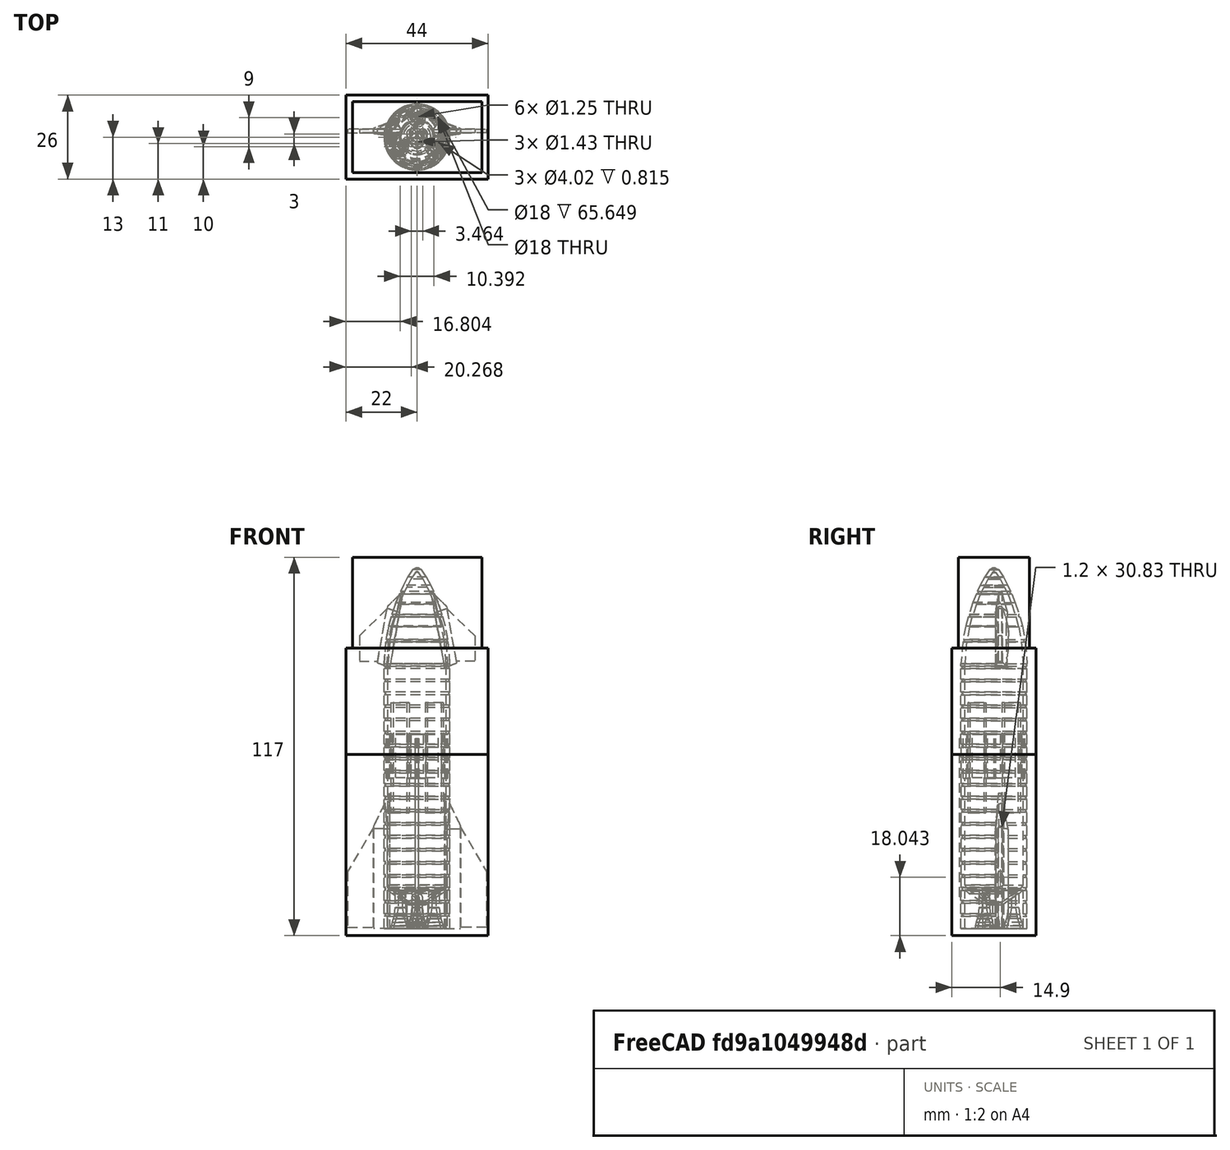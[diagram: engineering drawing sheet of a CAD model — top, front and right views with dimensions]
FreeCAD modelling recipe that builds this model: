
FCSTD DOCUMENT  (FreeCAD 0.18R16146 (Git))
Label: starship
License: All rights reserved
LicenseURL: http://en.wikipedia.org/wiki/All_rights_reserved
objects: Sketcher::SketchObject×14, Part::FeaturePython×5, Part::Box×5, Part::Extrusion×4, Part::Torus×4, Part::Revolution×4, Part::MultiFuse×4, Mesh::Feature×2, Part::Loft×2, Image::ImagePlane×1, Part::Cylinder×1, Part::Compound×1, PartDesign::FeatureBase×1, PartDesign::Body×1, Part::Mirroring×1, Part::Cut×1
note: 48 computed .brp shape members not serialized (recipe doc carries the construction recipe); baked Part::Feature solids carry a one-line shape summary decoded from their .brp

FEATURE [Mesh::Feature] SN8_Core
FEATURE [Mesh::Feature] SN8_Nose
  Placement = pos=(10.7,-34,-164.97) rot=(0,1,0;3.14159rad)
FEATURE [Image::ImagePlane] ImagePlane
  Placement = pos=(0,17,0) rot=(1,0,0;1.5708rad)
  XSize = 93
  YSize = 130
FEATURE [Sketcher::SketchObject] Sketch  label="fuse"
  Placement = pos=(0,0,0) rot=(1,0,0;1.5708rad)
  sketch-geometry (12):
    g0: LineSegment StartX=1.39017 StartY=57.1876 StartZ=0 EndX=2.9316 EndY=54.8754 EndZ=0
    g1: LineSegment StartX=5.37975 StartY=50.0245 StartZ=0 EndX=6.55849 EndY=46.987 EndZ=0
    g2: LineSegment StartX=6.55849 StartY=46.987 StartZ=0 EndX=7.91857 EndY=42.9067 EndZ=0
    g3: LineSegment StartX=7.91857 StartY=42.9067 StartZ=0 EndX=8.78321 EndY=39.8104 EndZ=0
    g4: LineSegment StartX=8.78321 StartY=39.8104 StartZ=0 EndX=9.64459 EndY=35.1408 EndZ=0
    g5: LineSegment StartX=9.64459 StartY=35.1408 StartZ=0 EndX=10.2 EndY=28.1137 EndZ=0
    g6: LineSegment StartX=10.2 StartY=28.1137 StartZ=0 EndX=10.2 EndY=25.3049 EndZ=0
    g7: LineSegment StartX=10.2 StartY=25.3049 StartZ=0 EndX=10.2 EndY=-53.7768 EndZ=0
    g8: LineSegment StartX=1.39017 StartY=57.1876 StartZ=0 EndX=0.452917 EndY=57.777 EndZ=0
    g9: LineSegment StartX=0.452917 StartY=57.777 StartZ=0 EndX=0 EndY=57.777 EndZ=0
    g10: LineSegment StartX=2.9316 StartY=54.8754 StartZ=0 EndX=4.24635 EndY=52.3366 EndZ=0
    g11: LineSegment StartX=4.24635 StartY=52.3366 StartZ=0 EndX=5.37975 EndY=50.0245 EndZ=0
  constraints (16):
    c: Coincident(g1,g2)
    c: Coincident(g2,g3)
    c: Coincident(g3,g4)
    c: Coincident(g4,g5)
    c: Coincident(g5,g6)
    c: Coincident(g6,g7)
    c: Vertical(g7)
    c: Coincident(g0,g8)
    c: Coincident(g8,g9)
    c: Horizontal(g9)
    c: Coincident(g0,g10)
    c: Coincident(g11,g1)
    c: Coincident(g10,g11)
    c: Vertical(g6)
    c: DistanceX(g-1,g7) = 10.2
    c: PointOnObject(g9,g-2)
FEATURE [Sketcher::SketchObject] Sketch001  label="bulkhead"
  Placement = pos=(0,0,0) rot=(-1,0,0;4.71239rad)
  sketch-geometry (5):
    g0: LineSegment StartX=10.1563 StartY=-38.9984 StartZ=0 EndX=9.76929 EndY=-40.6281 EndZ=0
    g1: LineSegment StartX=9.76929 StartY=-40.6281 StartZ=0 EndX=8.91371 EndY=-41.9522 EndZ=0
    g2: LineSegment StartX=8.91371 StartY=-41.9522 StartZ=0 EndX=7.7322 EndY=-42.9503 EndZ=0
    g3: LineSegment StartX=7.7322 StartY=-42.9503 StartZ=0 EndX=2.558 EndY=-46.4338 EndZ=0
    g4: LineSegment StartX=2.558 StartY=-46.4338 StartZ=0 EndX=0 EndY=-46.4338 EndZ=0
  constraints (6):
    c: Coincident(g0,g1)
    c: Coincident(g1,g2)
    c: Coincident(g2,g3)
    c: Coincident(g3,g4)
    c: Horizontal(g4)
    c: PointOnObject(g4,g-2)
FEATURE [Sketcher::SketchObject] Sketch002
  Placement = pos=(0,0,0) rot=(-1,0,0;4.71239rad)
  sketch-geometry (6):
    g0: LineSegment StartX=9.20478 StartY=45.2053 StartZ=0 EndX=17.8355 EndY=36.6962 EndZ=0
    g1: LineSegment StartX=17.8355 StartY=36.6962 StartZ=0 EndX=17.8355 EndY=28.9468 EndZ=0
    g2: LineSegment StartX=17.8355 StartY=28.9468 StartZ=0 EndX=12.0918 EndY=28.9468 EndZ=0
    g3: LineSegment StartX=12.0918 StartY=28.9468 StartZ=0 EndX=11.0282 EndY=28.7036 EndZ=0
    g4: LineSegment StartX=11.0282 StartY=28.7036 StartZ=0 EndX=7.9588 EndY=45.6004 EndZ=0
    g5: LineSegment StartX=7.9588 StartY=45.6004 StartZ=0 EndX=9.20478 EndY=45.2053 EndZ=0
  constraints (8):
    c: Coincident(g0,g1)
    c: Vertical(g1)
    c: Coincident(g1,g2)
    c: Horizontal(g2)
    c: Coincident(g2,g3)
    c: Coincident(g3,g4)
    c: Coincident(g4,g5)
    c: Coincident(g0,g5)
FEATURE [Part::Extrusion] Extrude  label="canard"
  Base = -> Sketch002
  Dir = (0,-1,0)
  DirMode = 2
  FaceMakerClass = Part::FaceMakerBullseye
  LengthFwd = 1.2
  LengthRev = 0
  Placement = pos=(0,2.5,0) rot=(0,0,1;0rad)
  Solid = true
  Symmetric = false
FEATURE [Sketcher::SketchObject] Sketch003
  Placement = pos=(0,0,0) rot=(-1,0,0;4.71239rad)
  sketch-geometry (5):
    g0: LineSegment StartX=11.6943 StartY=-21.9919 StartZ=0 EndX=13.1785 EndY=-21.9919 EndZ=0
    g1: LineSegment StartX=13.1785 StartY=-21.9919 StartZ=0 EndX=21.419 EndY=-36.1383 EndZ=0
    g2: LineSegment StartX=21.419 StartY=-36.1383 StartZ=0 EndX=21.419 EndY=-53.3693 EndZ=0
    g3: LineSegment StartX=21.419 StartY=-53.3693 StartZ=0 EndX=11.6943 EndY=-53.3693 EndZ=0
    g4: LineSegment StartX=11.6943 StartY=-53.3693 StartZ=0 EndX=11.6943 EndY=-21.9919 EndZ=0
  constraints (9):
    c: Horizontal(g0)
    c: Coincident(g0,g1)
    c: Coincident(g1,g2)
    c: Vertical(g2)
    c: Coincident(g2,g3)
    c: Horizontal(g3)
    c: Coincident(g3,g4)
    c: Coincident(g4,g0)
    c: Vertical(g4)
FEATURE [Part::Extrusion] Extrude001  label="wing"
  Base = -> Sketch003
  Dir = (0,-1,0)
  DirMode = 2
  FaceMakerClass = Part::FaceMakerBullseye
  LengthFwd = 1.2
  LengthRev = 0
  Placement = pos=(0,2.5,0) rot=(0,0,1;0rad)
  Solid = true
  Symmetric = false
FEATURE [Sketcher::SketchObject] Sketch004
  Placement = pos=(0,-20,0) rot=(-1,0,0;4.71239rad)
  sketch-geometry (6):
    g0: LineSegment StartX=0.961528 StartY=28.0137 StartZ=0 EndX=5.05356 EndY=28.0137 EndZ=0
    g1: LineSegment StartX=5.05356 StartY=28.0137 StartZ=0 EndX=5.05356 EndY=45.3257 EndZ=0
    g2: LineSegment StartX=5.05356 StartY=45.3257 StartZ=0 EndX=2.97627 EndY=52.0547 EndZ=0
    g3: LineSegment StartX=2.97627 StartY=52.0547 StartZ=0 EndX=2.01195 EndY=52.0547 EndZ=0
    g4: LineSegment StartX=2.01195 StartY=52.0547 StartZ=0 EndX=0.961528 EndY=45.3257 EndZ=0
    g5: LineSegment StartX=0.961528 StartY=45.3257 StartZ=0 EndX=0.961528 EndY=28.0137 EndZ=0
  constraints (11):
    c: Horizontal(g0)
    c: Coincident(g0,g1)
    c: Vertical(g1)
    c: Coincident(g1,g2)
    c: Coincident(g2,g3)
    c: Horizontal(g3)
    c: Coincident(g3,g4)
    c: Coincident(g4,g5)
    c: Coincident(g5,g0)
    c: Vertical(g5)
    c: Horizontal(g4,g1)
FEATURE [Sketcher::SketchObject] Sketch005
  Placement = pos=(0,-24,0) rot=(-1,0,0;4.71239rad)
  sketch-geometry (6):
    g0: LineSegment StartX=1.58391 StartY=28.793 StartZ=0 EndX=3.35398 EndY=28.793 EndZ=0
    g1: LineSegment StartX=3.35398 StartY=28.793 StartZ=0 EndX=3.35398 EndY=45.9466 EndZ=0
    g2: LineSegment StartX=3.35398 StartY=45.9466 StartZ=0 EndX=3 EndY=46.4936 EndZ=0
    g3: LineSegment StartX=3 StartY=46.4936 StartZ=0 EndX=1.97988 EndY=46.4936 EndZ=0
    g4: LineSegment StartX=1.97988 StartY=46.4936 StartZ=0 EndX=1.58391 EndY=45.9466 EndZ=0
    g5: LineSegment StartX=1.58391 StartY=45.9466 StartZ=0 EndX=1.58391 EndY=28.793 EndZ=0
  constraints (11):
    c: Horizontal(g0)
    c: Coincident(g0,g1)
    c: Vertical(g1)
    c: Coincident(g1,g2)
    c: Coincident(g2,g3)
    c: Horizontal(g3)
    c: Coincident(g3,g4)
    c: Coincident(g4,g5)
    c: Coincident(g5,g0)
    c: Vertical(g5)
    c: Horizontal(g4,g1)
FEATURE [Part::Loft] Loft
  Closed = false
  MaxDegree = 5
  Placement = pos=(-7,-0.6,-3) rot=(0,0,1;1.5708rad)
  Ruled = false
  Sections = -> [Sketch004,Sketch005]
  Solid = true
FEATURE [Sketcher::SketchObject] Sketch006
  Placement = pos=(0,-19,0) rot=(1,0,0;1.5708rad)
  sketch-geometry (6):
    g0: LineSegment StartX=1 StartY=-53.7958 StartZ=0 EndX=5.16679 EndY=-53.7958 EndZ=0
    g1: LineSegment StartX=5.16679 StartY=-53.7958 StartZ=0 EndX=5.16679 EndY=-23.0201 EndZ=0
    g2: LineSegment StartX=5.16679 StartY=-23.0201 StartZ=0 EndX=2.94225 EndY=-12.0034 EndZ=0
    g3: LineSegment StartX=2.94225 StartY=-12.0034 StartZ=0 EndX=1.9532 EndY=-12.0034 EndZ=0
    g4: LineSegment StartX=1.9532 StartY=-12.0034 StartZ=0 EndX=1 EndY=-23.0201 EndZ=0
    g5: LineSegment StartX=1 StartY=-23.0201 StartZ=0 EndX=1 EndY=-53.7958 EndZ=0
  constraints (11):
    c: Horizontal(g0)
    c: Coincident(g0,g1)
    c: Vertical(g1)
    c: Coincident(g1,g2)
    c: Coincident(g2,g3)
    c: Horizontal(g3)
    c: Coincident(g3,g4)
    c: Coincident(g4,g5)
    c: Coincident(g5,g0)
    c: Vertical(g5)
    c: Horizontal(g4,g1)
FEATURE [Sketcher::SketchObject] Sketch007
  Placement = pos=(0,-24,0) rot=(1,0,0;1.5708rad)
  sketch-geometry (6):
    g0: LineSegment StartX=1.66215 StartY=-53.7861 StartZ=0 EndX=3.30494 EndY=-53.7861 EndZ=0
    g1: LineSegment StartX=3.30494 StartY=-53.7861 StartZ=0 EndX=3.30494 EndY=-22.9295 EndZ=0
    g2: LineSegment StartX=3.30494 StartY=-22.9295 StartZ=0 EndX=2.99943 EndY=-22.214 EndZ=0
    g3: LineSegment StartX=2.99943 StartY=-22.214 StartZ=0 EndX=2.01296 EndY=-22.214 EndZ=0
    g4: LineSegment StartX=2.01296 StartY=-22.214 StartZ=0 EndX=1.66215 EndY=-22.9295 EndZ=0
    g5: LineSegment StartX=1.66215 StartY=-22.9295 StartZ=0 EndX=1.66215 EndY=-53.7861 EndZ=0
  constraints (11):
    c: Horizontal(g0)
    c: Coincident(g0,g1)
    c: Vertical(g1)
    c: Coincident(g1,g2)
    c: Coincident(g2,g3)
    c: Horizontal(g3)
    c: Coincident(g3,g4)
    c: Coincident(g4,g5)
    c: Coincident(g5,g0)
    c: Vertical(g5)
    c: Horizontal(g4,g1)
FEATURE [Part::Loft] Loft001  label="wing001"
  Closed = false
  MaxDegree = 5
  Placement = pos=(-10.5,-0.6,0) rot=(0,0,1;1.5708rad)
  Ruled = false
  Sections = -> [Sketch006,Sketch007]
  Solid = true
FEATURE [Part::Torus] Torus
  Angle1 = -180
  Angle2 = 180
  Angle3 = 360
  AttacherType = Attacher::AttachEngine3D
  Placement = pos=(0,0,-49.6) rot=(0,0,1;0rad)
  Radius1 = 10.2
  Radius2 = 0.4
FEATURE [Part::FeaturePython] Array  label="rings"  # Draft array (typed FeaturePython)
  Angle = 360
  ArrayType = 0
  Axis = (0,0,1)
  Base = -> Torus
  Center = (0,0,0)
  Fuse = false
  IntervalAxis = (0,0,0)
  IntervalX = (1,0,0)
  IntervalY = (0,1,0)
  IntervalZ = (0,0,4.03)
  NumberPolar = 1
  NumberX = 1
  NumberY = 1
  NumberZ = 20
FEATURE [Part::Torus] Torus001  label="ring3"
  Angle1 = -180
  Angle2 = 180
  Angle3 = 360
  AttacherType = Attacher::AttachEngine3D
  Placement = pos=(0,0,35.2) rot=(0,0,1;0rad)
  Radius1 = 9.6
  Radius2 = 0.4
FEATURE [Part::Torus] Torus002  label="ring2"
  Angle1 = -180
  Angle2 = 180
  Angle3 = 360
  AttacherType = Attacher::AttachEngine3D
  Placement = pos=(0,0,43) rot=(0,0,1;0rad)
  Radius1 = 7.9
  Radius2 = 0.4
FEATURE [Part::Torus] Torus003  label="ring1"
  Angle1 = -180
  Angle2 = 180
  Angle3 = 360
  AttacherType = Attacher::AttachEngine3D
  Placement = pos=(0,0,50.1) rot=(0,0,1;0rad)
  Radius1 = 5.3
  Radius2 = 0.4
FEATURE [Sketcher::SketchObject] Sketch008  label="raptor1"
  Placement = pos=(0,0,0) rot=(-1,0,0;4.71239rad)
  sketch-geometry (7):
    g0: LineSegment StartX=3.51528 StartY=-45.7778 StartZ=0 EndX=3.51528 EndY=-53.7953 EndZ=0
    g1: LineSegment StartX=3.51528 StartY=-45.7778 StartZ=0 EndX=2 EndY=-45.7778 EndZ=0
    g2: LineSegment StartX=2.71528 StartY=-53.7953 StartZ=0 EndX=3.51528 EndY=-53.7953 EndZ=0
    g3: LineSegment StartX=2.71528 StartY=-53.7953 StartZ=0 EndX=2.71528 EndY=-52.5604 EndZ=0
    g4: LineSegment StartX=2.71528 StartY=-52.5604 StartZ=0 EndX=2.47754 EndY=-51.0684 EndZ=0
    g5: LineSegment StartX=2.47754 StartY=-51.0684 StartZ=0 EndX=2 EndY=-50.2056 EndZ=0
    g6: LineSegment StartX=2 StartY=-45.7778 StartZ=0 EndX=2 EndY=-50.2056 EndZ=0
  constraints (14):
    c: Vertical(g0)
    c: Coincident(g0,g1)
    c: Horizontal(g1)
    c: Coincident(g2,g0)
    c: Horizontal(g2)
    c: DistanceX(g2,g0) = 0.8
    c: Coincident(g2,g3)
    c: Coincident(g3,g4)
    c: Coincident(g4,g5)
    c: Vertical(g3)
    c: Coincident(g6,g1)
    c: Coincident(g6,g5)
    c: Vertical(g6)
    c: DistanceX(g-1,g1) = 2
FEATURE [Part::Revolution] Revolve003
  Angle = 360
  Axis = (0,0,1)
  Base = (2,0,0)
  FaceMakerClass = Part::FaceMakerBullseye
  Solid = true
  Source = -> Sketch008
  Symmetric = false
FEATURE [Part::FeaturePython] Array001  label="engines001"  # Draft array (typed FeaturePython)
  Angle = 360
  ArrayType = 1
  Axis = (0,0,1)
  Base = -> Revolve003
  Center = (0,0,0)
  Fuse = false
  IntervalAxis = (0,0,0)
  IntervalX = (1,0,0)
  IntervalY = (0,1,0)
  IntervalZ = (0,0,1)
  NumberPolar = 3
  NumberX = 2
  NumberY = 2
  NumberZ = 1
  Placement = pos=(0,0,0) rot=(0,0,1;0.523599rad)
FEATURE [Sketcher::SketchObject] Sketch009  label="raptor2"
  Placement = pos=(0,0,0) rot=(-1,0,0;4.71239rad)
  sketch-geometry (14):
    g0: LineSegment StartX=8.62735 StartY=-42.0035 StartZ=0 EndX=8.62735 EndY=-47.3777 EndZ=0
    g1: LineSegment StartX=8.62735 StartY=-47.3777 StartZ=0 EndX=8.92762 EndY=-49.4325 EndZ=0
    g2: LineSegment StartX=8.92762 StartY=-49.4325 StartZ=0 EndX=9.20222 EndY=-50.7597 EndZ=0
    g3: LineSegment StartX=9.20222 StartY=-50.7597 StartZ=0 EndX=9.52258 EndY=-51.8672 EndZ=0
    g4: LineSegment StartX=9.52258 StartY=-51.8672 StartZ=0 EndX=9.81 EndY=-52.9257 EndZ=0
    g5: LineSegment StartX=9.81 StartY=-52.9257 StartZ=0 EndX=9.81 EndY=-53.7894 EndZ=0
    g6: LineSegment StartX=9.81 StartY=-53.7894 StartZ=0 EndX=9.01 EndY=-53.7894 EndZ=0
    g7: LineSegment StartX=7.62735 StartY=-42.0035 StartZ=0 EndX=8.62735 EndY=-42.0035 EndZ=0
    g8: LineSegment StartX=7.62735 StartY=-47.4589 StartZ=0 EndX=7.99399 EndY=-49.4782 EndZ=0
    g9: LineSegment StartX=7.99399 StartY=-49.4782 StartZ=0 EndX=8.26859 EndY=-50.8055 EndZ=0
    g10: LineSegment StartX=8.26859 StartY=-50.8055 StartZ=0 EndX=8.64387 EndY=-51.913 EndZ=0
    g11: LineSegment StartX=8.64387 StartY=-51.913 StartZ=0 EndX=9.01 EndY=-52.9748 EndZ=0
    g12: LineSegment StartX=9.01 StartY=-52.9748 StartZ=0 EndX=9.01 EndY=-53.7894 EndZ=0
    g13: LineSegment StartX=7.62735 StartY=-42.0035 StartZ=0 EndX=7.62735 EndY=-47.4589 EndZ=0
  constraints (22):
    c: Vertical(g0)
    c: Coincident(g1,g2)
    c: Coincident(g2,g3)
    c: Coincident(g3,g4)
    c: Coincident(g4,g5)
    c: Vertical(g5)
    c: Coincident(g5,g6)
    c: Horizontal(g6)
    c: Coincident(g7,g0)
    c: Horizontal(g7)
    c: Coincident(g8,g9)
    c: Coincident(g9,g10)
    c: Coincident(g10,g11)
    c: Coincident(g11,g12)
    c: Vertical(g12)
    c: Coincident(g6,g12)
    c: Coincident(g13,g7)
    c: Coincident(g13,g8)
    c: Vertical(g13)
    c: Coincident(g0,g1)
    c: DistanceX(g6,g5) = 0.8
    c: DistanceX(g7,g0) = 1
FEATURE [Part::Revolution] Revolve004
  Angle = 360
  Axis = (0,0,1)
  Base = (7,0,0)
  FaceMakerClass = Part::FaceMakerBullseye
  Placement = pos=(-1,0,0) rot=(0,0,1;0rad)
  Solid = true
  Source = -> Sketch009
  Symmetric = false
FEATURE [Part::FeaturePython] Array002  label="engines"  # Draft array (typed FeaturePython)
  Angle = 360
  ArrayType = 1
  Axis = (0,0,1)
  Base = -> Revolve004
  Center = (0,0,0)
  Fuse = false
  IntervalAxis = (0,0,0)
  IntervalX = (1,0,0)
  IntervalY = (0,1,0)
  IntervalZ = (0,0,1)
  NumberPolar = 3
  NumberX = 2
  NumberY = 2
  NumberZ = 1
  Placement = pos=(0,0,0) rot=(0,0,1;-0.523599rad)
FEATURE [Part::Box] Box  label="magnet"
  AttacherType = Attacher::AttachEngine3D
  Height = 13.3
  Length = 13.3
  Placement = pos=(-6.65,-6.65,-7) rot=(0,0,1;0rad)
  Width = 13.3
FEATURE [Part::Cylinder] Cylinder  label="pipe"
  Angle = 360
  AttacherType = Attacher::AttachEngine3D
  Height = 49
  Placement = pos=(0,-10.1,-44) rot=(0,0,1;0rad)
  Radius = 0.5
FEATURE [Part::Box] Box001  label="sub magnet"
  AttacherType = Attacher::AttachEngine3D
  Height = 13.5
  Length = 13.5
  Placement = pos=(0,-9.55,-7.25) rot=(0,0,1;0.785398rad)
  Width = 13.5
FEATURE [Part::MultiFuse] Fusion  label="rings001"
  Shapes = -> [Torus003,Torus001,Array,Torus002,Box001]
FEATURE [Part::Box] Box002  label="bottom print mask"
  AttacherType = Attacher::AttachEngine3D
  Height = 56
  Length = 44
  Placement = pos=(-22,-13,-56) rot=(0,0,1;0rad)
  Width = 26
FEATURE [Part::Compound] Compound
  Links = -> [Loft]
  Placement = pos=(0,0,0) rot=(0,1,0;6.10865rad)
FEATURE [Part::MultiFuse] Fusion002  label="right"
  Shapes = -> [Extrude,Extrude001,Loft001,Compound]
FEATURE [PartDesign::FeatureBase] Clone
  BaseFeature = -> Fusion002
FEATURE [PartDesign::Body] Body  label="right001"
  Group = -> [Clone]
  Origin = -> Origin
  Tip = -> Clone
FEATURE [Part::Mirroring] Part__Mirroring  label="left (Mirror #1)"
  Base = (-1.19209e-07,2.46416,-1.61446)
  Normal = (1,0,-1.19209e-07)
  Source = -> Body
FEATURE [Sketcher::SketchObject] Sketch010
  Placement = pos=(0,0,-60) rot=(-1,0,0;3.14159rad)
  sketch-geometry (4):
    g0: LineSegment StartX=-3.5 StartY=7 StartZ=0 EndX=3.5 EndY=7 EndZ=0
    g1: LineSegment StartX=-3.5 StartY=7.96492 StartZ=0 EndX=-3.5 EndY=7 EndZ=0
    g2: LineSegment StartX=3.5 StartY=7.96492 StartZ=0 EndX=3.5 EndY=7 EndZ=0
    g3: ArcOfCircle CenterX=0 CenterY=0 CenterZ=0 NormalX=0 NormalY=0 NormalZ=1 AngleXU=0 Radius=8.7 StartAngle=1.15677 EndAngle=1.98482
  constraints (12):
    c: Horizontal(g0)
    c: Vertical(g1)
    c: Vertical(g2)
    c: Coincident(g0,g1)
    c: Coincident(g0,g2)
    c: DistanceY(g-1,g0) = 7
    c: DistanceX(g-1,g0) = 3.5
    c: DistanceX(g0,g0) = 7
    c: Coincident(g3,g-1)
    c: Coincident(g3,g1)
    c: Coincident(g3,g2)
    c: Radius(g3) = 8.7
FEATURE [Part::Extrusion] Extrude002
  Base = -> Sketch010
  Dir = (0,1e-16,-1)
  DirMode = 2
  FaceMakerClass = Part::FaceMakerBullseye
  LengthFwd = 34
  LengthRev = 0
  Placement = pos=(0,0,76) rot=(0,0,1;0rad)
  Solid = true
  Symmetric = false
FEATURE [Part::FeaturePython] Array003  label="tabs"  # Draft array (typed FeaturePython)
  Angle = 360
  ArrayType = 1
  Axis = (0,0,1)
  Base = -> Extrude002
  Center = (0,0,0)
  Fuse = false
  IntervalAxis = (0,0,0)
  IntervalX = (1,0,0)
  IntervalY = (0,1,0)
  IntervalZ = (0,0,1)
  NumberPolar = 2
  NumberX = 2
  NumberY = 2
  NumberZ = 1
  Placement = pos=(0,0,0) rot=(0,0,1;0.785398rad)
FEATURE [Part::Box] Box003  label="top print mask"
  AttacherType = Attacher::AttachEngine3D
  Height = 28
  Length = 40
  Placement = pos=(-20,-11,33) rot=(0,0,1;0rad)
  Width = 22
FEATURE [Sketcher::SketchObject] fuse001
  Placement = pos=(0,0,0) rot=(1,0,0;1.5708rad)
  sketch-geometry (26):
    g0: LineSegment StartX=10.2 StartY=-53.7768 StartZ=0 EndX=10.2 EndY=25.3049 EndZ=0
    g1: LineSegment StartX=9 StartY=-53.7768 StartZ=0 EndX=9 EndY=25.3049 EndZ=0
    g2: LineSegment StartX=10.2 StartY=25.3049 StartZ=0 EndX=10.2 EndY=28.1137 EndZ=0
    g3: LineSegment StartX=9 StartY=25.3049 StartZ=0 EndX=9 EndY=28.0663 EndZ=0
    g4: LineSegment StartX=10.2 StartY=28.1137 StartZ=0 EndX=9.64459 EndY=35.1408 EndZ=0
    g5: LineSegment StartX=9 StartY=28.0663 StartZ=0 EndX=8.45322 EndY=34.9842 EndZ=0
    g6: LineSegment StartX=9.64459 StartY=35.1408 StartZ=0 EndX=8.78321 EndY=39.8104 EndZ=0
    g7: LineSegment StartX=8.45322 StartY=34.9842 StartZ=0 EndX=7.61291 EndY=39.5396 EndZ=0
    g8: LineSegment StartX=8.78321 StartY=39.8104 StartZ=0 EndX=7.91857 EndY=42.9067 EndZ=0
    g9: LineSegment StartX=7.61291 StartY=39.5396 StartZ=0 EndX=6.77077 EndY=42.5554 EndZ=0
    g10: LineSegment StartX=7.91857 StartY=42.9067 StartZ=0 EndX=6.55849 EndY=46.987 EndZ=0
    g11: LineSegment StartX=6.77077 StartY=42.5554 StartZ=0 EndX=5.42926 EndY=46.5799 EndZ=0
    g12: LineSegment StartX=6.55849 StartY=46.987 StartZ=0 EndX=5.37975 EndY=50.0245 EndZ=0
    g13: LineSegment StartX=5.42926 StartY=46.5799 StartZ=0 EndX=4.27963 EndY=49.5424 EndZ=0
    g14: LineSegment StartX=5.37975 StartY=50.0245 StartZ=0 EndX=4.24635 EndY=52.3366 EndZ=0
    g15: LineSegment StartX=4.27963 StartY=49.5424 StartZ=0 EndX=3.17467 EndY=51.7965 EndZ=0
    g16: LineSegment StartX=4.24635 StartY=52.3366 StartZ=0 EndX=2.9316 EndY=54.8754 EndZ=0
    g17: LineSegment StartX=3.17467 StartY=51.7965 StartZ=0 EndX=1.89644 EndY=54.2649 EndZ=0
    g18: LineSegment StartX=2.9316 StartY=54.8754 StartZ=0 EndX=1.39017 EndY=57.1876 EndZ=0
    g19: LineSegment StartX=1.89644 StartY=54.2649 StartZ=0 EndX=0.534094 EndY=56.3084 EndZ=0
    g20: LineSegment StartX=1.39017 StartY=57.1876 StartZ=0 EndX=0.452917 EndY=57.777 EndZ=0
    g21: LineSegment StartX=0.534094 StartY=56.3084 StartZ=0 EndX=0.106983 EndY=56.577 EndZ=0
    g22: LineSegment StartX=0.452917 StartY=57.777 StartZ=0 EndX=0 EndY=57.777 EndZ=0
    g23: LineSegment StartX=0.106983 StartY=56.577 StartZ=0 EndX=-2e-16 EndY=56.577 EndZ=0
    g24: LineSegment StartX=10.2 StartY=-53.7768 StartZ=0 EndX=9 EndY=-53.7768 EndZ=0
    g25: LineSegment StartX=0 StartY=57.777 StartZ=0 EndX=-2e-16 EndY=56.577 EndZ=0
FEATURE [Part::Revolution] Revolve007
  Angle = 360
  Axis = (0,0,1)
  Base = (0,0,0)
  FaceMakerClass = Part::FaceMakerBullseye
  Solid = true
  Source = -> fuse001
  Symmetric = false
FEATURE [Sketcher::SketchObject] bulkhead  label="bulkhead001"
  Placement = pos=(0,0,0) rot=(1,0,0;1.5708rad)
  sketch-geometry (12):
    g0: LineSegment StartX=10.1563 StartY=-38.9984 StartZ=0 EndX=9.76929 EndY=-40.6281 EndZ=0
    g1: LineSegment StartX=9.37798 StartY=-38.8135 StartZ=0 EndX=9.02272 EndY=-40.3094 EndZ=0
    g2: LineSegment StartX=9.76929 StartY=-40.6281 StartZ=0 EndX=8.91371 EndY=-41.9522 EndZ=0
    g3: LineSegment StartX=9.02272 StartY=-40.3094 StartZ=0 EndX=8.30643 EndY=-41.4179 EndZ=0
    g4: LineSegment StartX=8.91371 StartY=-41.9522 StartZ=0 EndX=7.7322 EndY=-42.9503 EndZ=0
    g5: LineSegment StartX=8.30643 StartY=-41.4179 StartZ=0 EndX=7.24925 EndY=-42.3111 EndZ=0
    g6: LineSegment StartX=7.7322 StartY=-42.9503 StartZ=0 EndX=2.558 EndY=-46.4338 EndZ=0
    g7: LineSegment StartX=7.24925 StartY=-42.3111 StartZ=0 EndX=2.3138 EndY=-45.6338 EndZ=0
    g8: LineSegment StartX=2.558 StartY=-46.4338 StartZ=0 EndX=0 EndY=-46.4338 EndZ=0
    g9: LineSegment StartX=2.3138 StartY=-45.6338 StartZ=0 EndX=0 EndY=-45.6338 EndZ=0
    g10: LineSegment StartX=10.1563 StartY=-38.9984 StartZ=0 EndX=9.37798 EndY=-38.8135 EndZ=0
    g11: LineSegment StartX=0 StartY=-46.4338 StartZ=0 EndX=0 EndY=-45.6338 EndZ=0
FEATURE [Part::Revolution] Revolve  label="bulkhead002"
  Angle = 360
  Axis = (0,0,1)
  Base = (0,0,0)
  FaceMakerClass = Part::FaceMakerBullseye
  Solid = true
  Source = -> bulkhead
  Symmetric = false
FEATURE [Sketcher::SketchObject] Sketch011
  Placement = pos=(0,0,-60) rot=(-1,0,0;3.14159rad)
  sketch-geometry (8):
    g0: LineSegment StartX=-6 StartY=6.75 StartZ=0 EndX=-4 EndY=6.75 EndZ=0
    g1: LineSegment StartX=-4 StartY=6.75 StartZ=0 EndX=-4 EndY=8 EndZ=0
    g2: LineSegment StartX=-4 StartY=8 StartZ=0 EndX=-6 EndY=8 EndZ=0
    g3: LineSegment StartX=-6 StartY=8 StartZ=0 EndX=-6 EndY=6.75 EndZ=0
    g4: LineSegment StartX=-6.75 StartY=6 StartZ=0 EndX=-8 EndY=6 EndZ=0
    g5: LineSegment StartX=-8 StartY=6 StartZ=0 EndX=-8 EndY=4 EndZ=0
    g6: LineSegment StartX=-8 StartY=4 StartZ=0 EndX=-6.75 EndY=4 EndZ=0
    g7: LineSegment StartX=-6.75 StartY=4 StartZ=0 EndX=-6.75 EndY=6 EndZ=0
  constraints (24):
    c: Coincident(g0,g1)
    c: Coincident(g1,g2)
    c: Coincident(g2,g3)
    c: Coincident(g3,g0)
    c: Horizontal(g0)
    c: Horizontal(g2)
    c: Vertical(g1)
    c: Vertical(g3)
    c: DistanceX(g0,g-1) = 4
    c: DistanceY(g-1,g0) = 6.75
    c: DistanceY(g1) = 8
    c: DistanceX(g2,g1) = 2
    c: Coincident(g4,g5)
    c: Coincident(g5,g6)
    c: Coincident(g6,g7)
    c: Coincident(g7,g4)
    c: Horizontal(g4)
    c: Horizontal(g6)
    c: Vertical(g5)
    c: Vertical(g7)
    c: DistanceX(g4) = -6.75
    c: DistanceY(g4) = 6
    c: DistanceY(g5,g4) = 2
    c: DistanceX(g5,g-1) = 8
FEATURE [Part::Extrusion] Extrude003
  Base = -> Sketch011
  Dir = (0,1e-16,-1)
  DirMode = 2
  FaceMakerClass = Part::FaceMakerBullseye
  LengthFwd = 13.5
  LengthRev = 0
  Solid = true
  Symmetric = false
FEATURE [Part::FeaturePython] Array004  label="magnet support"  # Draft array (typed FeaturePython)
  Angle = 360
  ArrayType = 1
  Axis = (0,0,1)
  Base = -> Extrude003
  Center = (0,0,0)
  Fuse = false
  IntervalAxis = (0,0,0)
  IntervalX = (1,0,0)
  IntervalY = (0,1,0)
  IntervalZ = (0,0,1)
  NumberPolar = 4
  NumberX = 2
  NumberY = 2
  NumberZ = 1
  Placement = pos=(0,0,66.25) rot=(0,0,1;0.785398rad)
FEATURE [Part::MultiFuse] Fusion005
  Shapes = -> [Revolve007,Array004]
FEATURE [Part::Cut] Cut  label="fuse002"
  Base = -> Fusion005
  Tool = -> Fusion
FEATURE [Part::MultiFuse] Fusion006
  Shapes = -> [Array002,Cut,Cylinder,Revolve,Part__Mirroring,Fusion002,Array001]
FEATURE [Part::Box] Box004  label="mid print mask001"
  AttacherType = Attacher::AttachEngine3D
  Height = 33
  Length = 44
  Placement = pos=(-22,-13,0) rot=(0,0,1;0rad)
  Width = 26
